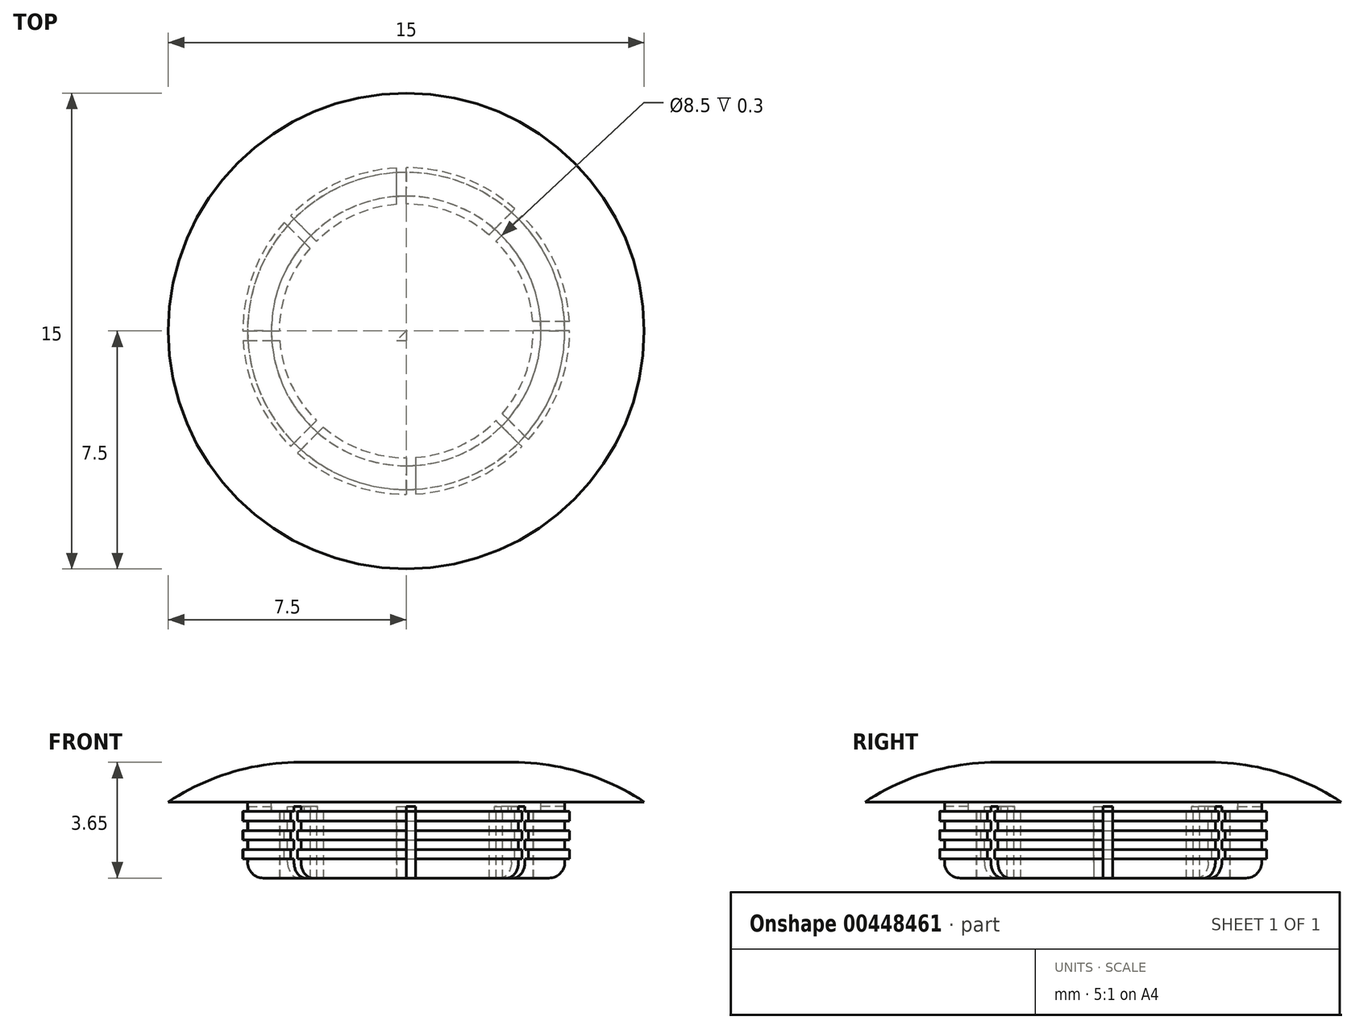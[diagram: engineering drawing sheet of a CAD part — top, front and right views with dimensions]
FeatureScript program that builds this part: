
annotation { "Feature Type Name" : "Feature", "Feature Type Description" : "" }
export const myFeature = defineFeature(function(context is Context, id is Id, definition is map)
    precondition{}
    {
        {
            var Q0;
            Q0=qCreatedBy(makeId("Top.planeOp"),FACE);
            var sketch = newSketch(context, id + "F0", { "sketchPlane" : qUnion([Q0])});
            skCircle(sketch, "E0", {"center": v(0, 0) * mm, "radius": 7.5 * mm});
            skCircle(sketch, "E1", {"center": v(0, 0) * mm, "radius": 5 * mm});
            skCircle(sketch, "E2", {"center": v(0, 0) * mm, "radius": 4.25 * mm});
            skSolve(sketch);
        }
        {
            var Q0;
            Q0=makeQuery(id+"F0.imprint","IMPRINT",FACE,{"disambiguationData":[TD([[makeQuery(id+"F0.imprint","IMPRINT",EDGE,{"derivedFrom":sQuery(id+"F0.wireOp",EDGE,"E0")}),1.0]])]});
            var Q1;
            Q1=makeQuery(id+"F0.imprint","IMPRINT",FACE,{"disambiguationData":[TD([[makeQuery(id+"F0.imprint","IMPRINT",EDGE,{"derivedFrom":sQuery(id+"F0.wireOp",EDGE,"E1")}),1.0]])]});
            var Q2;
            Q2=makeQuery(id+"F0.imprint","IMPRINT",FACE,{"disambiguationData":[TD([[makeQuery(id+"F0.imprint","IMPRINT",EDGE,{"derivedFrom":sQuery(id+"F0.wireOp",EDGE,"E2")}),1.0]])]});
            extrude(context, id + "F1", {"entities" : qUnion([Q0, Q1, Q2]), "depth" : 1.25 * mm});
        }
        {
            var Q0;
            Q0=makeQuery(id+"F1.opExtrude","CAP_EDGE",EDGE,{"disambiguationData":[OSD([sQuery(id+"F0.wireOp",EDGE,"E0")])],"isStart":false});
            fillet(context, id + "F2", {"entities" : qUnion([Q0]), "radius" : 7.5 * mm, "tangentPropagation" : true, "allowEdgeOverflow" : false});
        }
        {
            var Q0;
            Q0=makeQuery(id+"F0.imprint","IMPRINT",FACE,{"disambiguationData":[TD([[makeQuery(id+"F0.imprint","IMPRINT",EDGE,{"derivedFrom":sQuery(id+"F0.wireOp",EDGE,"E1")}),1.0]])]});
            extrude(context, id + "F3", {"entities" : qUnion([Q0]), "operationType" : NewBodyOperationType.ADD, "oppositeDirection" : true, "depth" : .3 * mm});
        }
        {
            var Q0;
            Q0=makeQuery(id+"F3.opExtrude","CAP_FACE",FACE,{"disambiguationData":[OSD([sQuery(id+"F0.wireOp",EDGE,"E1"),sQuery(id+"F0.wireOp",EDGE,"E2")])],"isStart":false});
            var sketch = newSketch(context, id + "F4", { "sketchPlane" : qUnion([Q0])});
            skCircle(sketch, "E3", {"center": v(0, 0) * mm, "radius": 5.15 * mm});
            skSolve(sketch);
        }
        {
            var Q0;
            Q0 = qSketchRegion(id + "F4", true);
            extrude(context, id + "F5", {"entities" : qUnion([Q0]), "operationType" : NewBodyOperationType.ADD, "depth" : .3 * mm});
        }
        {
            var Q0;
            Q0=makeQuery(id+"F5.opExtrude","CAP_FACE",FACE,{"disambiguationData":[OSD([sQuery(id+"F4.wireOp",EDGE,"E3")])],"isStart":false});
            var sketch = newSketch(context, id + "F6", { "sketchPlane" : qUnion([Q0])});
            skCircle(sketch, "E4", {"center": v(0, 0) * mm, "radius": 5 * mm});
            skSolve(sketch);
        }
        {
            var Q0;
            Q0 = qSketchRegion(id + "F6", true);
            extrude(context, id + "F7", {"entities" : qUnion([Q0]), "operationType" : NewBodyOperationType.ADD, "depth" : .3 * mm});
        }
        {
            var Q0;
            Q0=makeQuery(id+"F7.opExtrude","CAP_FACE",FACE,{"disambiguationData":[OSD([sQuery(id+"F6.wireOp",EDGE,"E4")])],"isStart":false});
            var sketch = newSketch(context, id + "F8", { "sketchPlane" : qUnion([Q0])});
            skCircle(sketch, "E5", {"center": v(0, 0) * mm, "radius": 5.15 * mm});
            skSolve(sketch);
        }
        {
            var Q0;
            Q0 = qSketchRegion(id + "F8", true);
            extrude(context, id + "F9", {"entities" : qUnion([Q0]), "operationType" : NewBodyOperationType.ADD, "depth" : .3 * mm});
        }
        {
            var Q0;
            Q0=makeQuery(id+"F9.opExtrude","CAP_FACE",FACE,{"disambiguationData":[OSD([sQuery(id+"F8.wireOp",EDGE,"E5")])],"isStart":false});
            var sketch = newSketch(context, id + "F10", { "sketchPlane" : qUnion([Q0])});
            skCircle(sketch, "E6", {"center": v(0, 0) * mm, "radius": 5 * mm});
            skSolve(sketch);
        }
        {
            var Q0;
            Q0 = qSketchRegion(id + "F10", true);
            extrude(context, id + "F11", {"entities" : qUnion([Q0]), "operationType" : NewBodyOperationType.ADD, "depth" : .3 * mm});
        }
        {
            var Q0;
            Q0=makeQuery(id+"F11.opExtrude","CAP_FACE",FACE,{"disambiguationData":[OSD([sQuery(id+"F10.wireOp",EDGE,"E6")])],"isStart":false});
            var sketch = newSketch(context, id + "F12", { "sketchPlane" : qUnion([Q0])});
            skCircle(sketch, "E7", {"center": v(0, 0) * mm, "radius": 5.15 * mm});
            skSolve(sketch);
        }
        {
            var Q0;
            Q0 = qSketchRegion(id + "F12", true);
            extrude(context, id + "F13", {"entities" : qUnion([Q0]), "operationType" : NewBodyOperationType.ADD, "depth" : .3 * mm});
        }
        {
            var Q0;
            Q0=makeQuery(id+"F13.opExtrude","CAP_FACE",FACE,{"disambiguationData":[OSD([sQuery(id+"F12.wireOp",EDGE,"E7")])],"isStart":false});
            var sketch = newSketch(context, id + "F14", { "sketchPlane" : qUnion([Q0])});
            skCircle(sketch, "E8", {"center": v(0, 0) * mm, "radius": 5 * mm});
            skSolve(sketch);
        }
        {
            var Q0;
            Q0 = qSketchRegion(id + "F14", true);
            extrude(context, id + "F15", {"entities" : qUnion([Q0]), "operationType" : NewBodyOperationType.ADD, "depth" : .6 * mm});
        }
        {
            var Q0;
            Q0=makeQuery(id+"F15.opExtrude","CAP_FACE",FACE,{"disambiguationData":[OSD([sQuery(id+"F14.wireOp",EDGE,"E8")])],"isStart":false});
            fillet(context, id + "F16", {"entities" : qUnion([Q0]), "radius" : .5 * mm, "tangentPropagation" : true, "allowEdgeOverflow" : false});
        }
        {
            var Q0;
            Q0=makeQuery(id+"F15.opExtrude","CAP_FACE",FACE,{"disambiguationData":[OSD([sQuery(id+"F14.wireOp",EDGE,"E8")])],"isStart":false});
            var sketch = newSketch(context, id + "F17", { "sketchPlane" : qUnion([Q0])});
            skCircle(sketch, "E9", {"center": v(0, 0) * mm, "radius": 4 * mm});
            skLineSegment(sketch, "E10", {"start": v(0, 0) * mm, "end": v(0, 6) * mm});
            skLineSegment(sketch, "E11", {"start": v(0, 0) * mm, "end": v(-4.24, 4.24) * mm});
            skLineSegment(sketch, "E12", {"start": v(-4.24, 4.24) * mm, "end": v(0, 0) * mm});
            skLineSegment(sketch, "E13", {"start": v(-6, 0) * mm, "end": v(0, 0) * mm});
            skLineSegment(sketch, "E14.MirrorCS", {"start": v(0, 0) * mm, "end": v(0, -6) * mm});
            skLineSegment(sketch, "E15.MirrorCS", {"start": v(-4.24, -4.24) * mm, "end": v(0, 0) * mm});
            skLineSegment(sketch, "E16.MirrorCS", {"start": v(4.24, 4.24) * mm, "end": v(0, 0) * mm});
            skLineSegment(sketch, "E17.MirrorCS", {"start": v(6, 0) * mm, "end": v(0, 0) * mm});
            skLineSegment(sketch, "E18.MirrorCS", {"start": v(4.24, -4.24) * mm, "end": v(0, 0) * mm});
            skLineSegment(sketch, "E19.0", {"start": v(0.3, 0) * mm, "end": v(0.3, 6) * mm});
            skLineSegment(sketch, "E20.0", {"start": v(6, -0.3) * mm, "end": v(0, -0.3) * mm});
            skLineSegment(sketch, "E21.0", {"start": v(4.03, -4.45) * mm, "end": v(-0.21, -0.21) * mm});
            skLineSegment(sketch, "E22.0", {"start": v(-0.3, 0) * mm, "end": v(-0.3, -6) * mm});
            skLineSegment(sketch, "E23.0", {"start": v(-4.45, -4.03) * mm, "end": v(-0.21, 0.21) * mm});
            skLineSegment(sketch, "E24.0", {"start": v(-6, 0.3) * mm, "end": v(0, 0.3) * mm});
            skLineSegment(sketch, "E25.0", {"start": v(-4.03, 4.45) * mm, "end": v(0.21, 0.21) * mm});
            skLineSegment(sketch, "E26.0", {"start": v(4.45, 4.03) * mm, "end": v(0.21, -0.21) * mm});
            skLineSegment(sketch, "E27", {"start": v(-4.24, 4.24) * mm, "end": v(-4.03, 4.45) * mm});
            skLineSegment(sketch, "E28", {"start": v(0, 6) * mm, "end": v(0.3, 6) * mm});
            skLineSegment(sketch, "E29", {"start": v(4.24, 4.24) * mm, "end": v(4.45, 4.03) * mm});
            skLineSegment(sketch, "E30", {"start": v(6, 0) * mm, "end": v(6, -0.3) * mm});
            skLineSegment(sketch, "E31", {"start": v(4.24, -4.24) * mm, "end": v(4.03, -4.45) * mm});
            skLineSegment(sketch, "E32", {"start": v(0, -6) * mm, "end": v(-0.3, -6) * mm});
            skLineSegment(sketch, "E33", {"start": v(-4.24, -4.24) * mm, "end": v(-4.45, -4.03) * mm});
            skLineSegment(sketch, "E34", {"start": v(-6, 0) * mm, "end": v(-6, 0.3) * mm});
            skSolve(sketch);
        }
        {
            var Q0;
            Q0=makeQuery(id+"F17.imprint","IMPRINT",FACE,{"disambiguationData":[TD([[makeQuery(id+"F17.imprint","IMPRINT",EDGE,{"derivedFrom":sQuery(id+"F17.wireOp",EDGE,"E9")}),1.0]])]});
            var Q1;
            {var subQ1=sQuery(id+"F17.wireOp",EDGE,"E9");var subQ7=sQuery(id+"F17.wireOp",EDGE,"E25.0");var subQ9=makeQuery(id+"F17.imprint","INTERSECT",VERTEX,{"derivedFrom":[subQ1,subQ7]});Q1=makeQuery(id+"F17.imprint","IMPRINT",FACE,{"disambiguationData":[TD([[makeQuery(id+"F17.imprint","IMPRINT",EDGE,{"disambiguationData":[TD([[subQ9,-1.0]])],"derivedFrom":subQ1}),1.0]])]});}
            var Q2;
            {var subQ0=sQuery(id+"F17.wireOp",EDGE,"E19.0");var subQ1=sQuery(id+"F17.wireOp",EDGE,"E9");var subQ2=makeQuery(id+"F17.imprint","INTERSECT",VERTEX,{"derivedFrom":[subQ1,subQ0]});Q2=makeQuery(id+"F17.imprint","IMPRINT",FACE,{"disambiguationData":[TD([[makeQuery(id+"F17.imprint","IMPRINT",EDGE,{"disambiguationData":[TD([[subQ2,-1.0]])],"derivedFrom":subQ1}),1.0]])]});}
            var Q3;
            {var subQ5=sQuery(id+"F17.wireOp",EDGE,"E9");var subQ7=sQuery(id+"F17.wireOp",EDGE,"E26.0");var subQ8=makeQuery(id+"F17.imprint","INTERSECT",VERTEX,{"derivedFrom":[subQ5,subQ7]});Q3=makeQuery(id+"F17.imprint","IMPRINT",FACE,{"disambiguationData":[TD([[makeQuery(id+"F17.imprint","IMPRINT",EDGE,{"disambiguationData":[TD([[subQ8,-1.0]])],"derivedFrom":subQ5}),1.0]])]});}
            var Q4;
            {var subQ1=sQuery(id+"F17.wireOp",EDGE,"E9");var subQ5=sQuery(id+"F17.wireOp",EDGE,"E17.MirrorCS");var subQ6=makeQuery(id+"F17.imprint","INTERSECT",VERTEX,{"derivedFrom":[subQ1,subQ5]});Q4=makeQuery(id+"F17.imprint","IMPRINT",FACE,{"disambiguationData":[TD([[makeQuery(id+"F17.imprint","IMPRINT",EDGE,{"disambiguationData":[TD([[subQ6,1.0]])],"derivedFrom":subQ1}),1.0]])]});}
            var Q5;
            {var subQ1=sQuery(id+"F17.wireOp",EDGE,"E9");var subQ7=sQuery(id+"F17.wireOp",EDGE,"E21.0");var subQ9=makeQuery(id+"F17.imprint","INTERSECT",VERTEX,{"derivedFrom":[subQ1,subQ7]});Q5=makeQuery(id+"F17.imprint","IMPRINT",FACE,{"disambiguationData":[TD([[makeQuery(id+"F17.imprint","IMPRINT",EDGE,{"disambiguationData":[TD([[subQ9,-1.0]])],"derivedFrom":subQ1}),1.0]])]});}
            var Q6;
            {var subQ3=sQuery(id+"F17.wireOp",EDGE,"E22.0");var subQ7=sQuery(id+"F17.wireOp",EDGE,"E9");var subQ9=makeQuery(id+"F17.imprint","INTERSECT",VERTEX,{"derivedFrom":[subQ7,subQ3]});Q6=makeQuery(id+"F17.imprint","IMPRINT",FACE,{"disambiguationData":[TD([[makeQuery(id+"F17.imprint","IMPRINT",EDGE,{"disambiguationData":[TD([[subQ9,-1.0]])],"derivedFrom":subQ7}),1.0]])]});}
            var Q7;
            {var subQ5=sQuery(id+"F17.wireOp",EDGE,"E9");var subQ7=sQuery(id+"F17.wireOp",EDGE,"E23.0");var subQ9=makeQuery(id+"F17.imprint","INTERSECT",VERTEX,{"derivedFrom":[subQ5,subQ7]});Q7=makeQuery(id+"F17.imprint","IMPRINT",FACE,{"disambiguationData":[TD([[makeQuery(id+"F17.imprint","IMPRINT",EDGE,{"disambiguationData":[TD([[subQ9,-1.0]])],"derivedFrom":subQ5}),1.0]])]});}
            var Q8;
            {var subQ1=sQuery(id+"F17.wireOp",EDGE,"E9");var subQ7=sQuery(id+"F17.wireOp",EDGE,"E24.0");var subQ8=makeQuery(id+"F17.imprint","INTERSECT",VERTEX,{"derivedFrom":[subQ1,subQ7]});Q8=makeQuery(id+"F17.imprint","IMPRINT",FACE,{"disambiguationData":[TD([[makeQuery(id+"F17.imprint","IMPRINT",EDGE,{"disambiguationData":[TD([[subQ8,-1.0]])],"derivedFrom":subQ1}),1.0]])]});}
            var Q9;
            {var subQ0=sQuery(id+"F17.wireOp",EDGE,"E17.MirrorCS");var subQ1=makeQuery(id+"F17.imprint","INTERSECT",VERTEX,{"derivedFrom":[subQ0,sQuery(id+"F17.wireOp",EDGE,"E19.0")]});Q9=makeQuery(id+"F17.imprint","IMPRINT",FACE,{"disambiguationData":[TD([[makeQuery(id+"F17.imprint","IMPRINT",EDGE,{"disambiguationData":[TD([[subQ1,1.0]])],"derivedFrom":subQ0}),1.0]])]});}
            var Q10;
            {var subQ0=sQuery(id+"F17.wireOp",EDGE,"E16.MirrorCS");var subQ1=makeQuery(id+"F17.imprint","INTERSECT",VERTEX,{"derivedFrom":[subQ0,sQuery(id+"F17.wireOp",EDGE,"E25.0")]});Q10=makeQuery(id+"F17.imprint","IMPRINT",FACE,{"disambiguationData":[TD([[makeQuery(id+"F17.imprint","IMPRINT",EDGE,{"disambiguationData":[TD([[subQ1,1.0]])],"derivedFrom":subQ0}),1.0]])]});}
            var Q11;
            {var subQ1=sQuery(id+"F17.wireOp",EDGE,"E10");var subQ3=makeQuery(id+"F17.imprint","INTERSECT",VERTEX,{"derivedFrom":[subQ1,sQuery(id+"F17.wireOp",EDGE,"E24.0")]});Q11=makeQuery(id+"F17.imprint","IMPRINT",FACE,{"disambiguationData":[TD([[makeQuery(id+"F17.imprint","IMPRINT",EDGE,{"disambiguationData":[TD([[subQ3,-1.0]])],"derivedFrom":subQ1}),-1.0]])]});}
            var Q12;
            {var subQ0=sQuery(id+"F17.wireOp",EDGE,"E12");var subQ5=makeQuery(id+"F17.imprint","INTERSECT",VERTEX,{"derivedFrom":[subQ0,sQuery(id+"F17.wireOp",EDGE,"E23.0")]});Q12=makeQuery(id+"F17.imprint","IMPRINT",FACE,{"disambiguationData":[TD([[makeQuery(id+"F17.imprint","IMPRINT",EDGE,{"disambiguationData":[TD([[subQ5,1.0]])],"derivedFrom":subQ0}),1.0]])]});}
            var Q13;
            {var subQ0=sQuery(id+"F17.wireOp",EDGE,"E13");var subQ5=makeQuery(id+"F17.imprint","INTERSECT",VERTEX,{"derivedFrom":[subQ0,sQuery(id+"F17.wireOp",EDGE,"E22.0")]});Q13=makeQuery(id+"F17.imprint","IMPRINT",FACE,{"disambiguationData":[TD([[makeQuery(id+"F17.imprint","IMPRINT",EDGE,{"disambiguationData":[TD([[subQ5,1.0]])],"derivedFrom":subQ0}),1.0]])]});}
            var Q14;
            {var subQ0=sQuery(id+"F17.wireOp",EDGE,"E15.MirrorCS");var subQ6=makeQuery(id+"F17.imprint","INTERSECT",VERTEX,{"derivedFrom":[subQ0,sQuery(id+"F17.wireOp",EDGE,"E21.0")]});Q14=makeQuery(id+"F17.imprint","IMPRINT",FACE,{"disambiguationData":[TD([[makeQuery(id+"F17.imprint","IMPRINT",EDGE,{"disambiguationData":[TD([[subQ6,1.0]])],"derivedFrom":subQ0}),1.0]])]});}
            var Q15;
            {var subQ1=sQuery(id+"F17.wireOp",EDGE,"E14.MirrorCS");var subQ3=makeQuery(id+"F17.imprint","INTERSECT",VERTEX,{"derivedFrom":[subQ1,sQuery(id+"F17.wireOp",EDGE,"E20.0")]});Q15=makeQuery(id+"F17.imprint","IMPRINT",FACE,{"disambiguationData":[TD([[makeQuery(id+"F17.imprint","IMPRINT",EDGE,{"disambiguationData":[TD([[subQ3,-1.0]])],"derivedFrom":subQ1}),-1.0]])]});}
            var Q16;
            {var subQ0=sQuery(id+"F17.wireOp",EDGE,"E18.MirrorCS");var subQ6=makeQuery(id+"F17.imprint","INTERSECT",VERTEX,{"derivedFrom":[subQ0,sQuery(id+"F17.wireOp",EDGE,"E26.0")]});Q16=makeQuery(id+"F17.imprint","IMPRINT",FACE,{"disambiguationData":[TD([[makeQuery(id+"F17.imprint","IMPRINT",EDGE,{"disambiguationData":[TD([[subQ6,1.0]])],"derivedFrom":subQ0}),1.0]])]});}
            var Q17;
            {var subQ0=sQuery(id+"F17.wireOp",EDGE,"E27");Q17=makeQuery(id+"F17.imprint","IMPRINT",FACE,{"disambiguationData":[TD([[makeQuery(id+"F17.imprint","IMPRINT",EDGE,{"derivedFrom":subQ0}),-1.0]])]});}
            var Q18;
            {var subQ0=sQuery(id+"F17.wireOp",EDGE,"E25.0");var subQ1=sQuery(id+"F17.wireOp",EDGE,"E9");var subQ2=makeQuery(id+"F17.imprint","INTERSECT",VERTEX,{"derivedFrom":[subQ1,subQ0]});Q18=makeQuery(id+"F17.imprint","IMPRINT",FACE,{"disambiguationData":[TD([[makeQuery(id+"F17.imprint","IMPRINT",EDGE,{"disambiguationData":[TD([[subQ2,-1.0]])],"derivedFrom":subQ1}),-1.0]])]});}
            var Q19;
            {var subQ0=sQuery(id+"F17.wireOp",EDGE,"E34");Q19=makeQuery(id+"F17.imprint","IMPRINT",FACE,{"disambiguationData":[TD([[makeQuery(id+"F17.imprint","IMPRINT",EDGE,{"derivedFrom":subQ0}),-1.0]])]});}
            var Q20;
            {var subQ0=sQuery(id+"F17.wireOp",EDGE,"E24.0");var subQ1=sQuery(id+"F17.wireOp",EDGE,"E9");var subQ2=makeQuery(id+"F17.imprint","INTERSECT",VERTEX,{"derivedFrom":[subQ1,subQ0]});Q20=makeQuery(id+"F17.imprint","IMPRINT",FACE,{"disambiguationData":[TD([[makeQuery(id+"F17.imprint","IMPRINT",EDGE,{"disambiguationData":[TD([[subQ2,-1.0]])],"derivedFrom":subQ1}),-1.0]])]});}
            var Q21;
            {var subQ0=sQuery(id+"F17.wireOp",EDGE,"E33");Q21=makeQuery(id+"F17.imprint","IMPRINT",FACE,{"disambiguationData":[TD([[makeQuery(id+"F17.imprint","IMPRINT",EDGE,{"derivedFrom":subQ0}),-1.0]])]});}
            var Q22;
            {var subQ0=sQuery(id+"F17.wireOp",EDGE,"E23.0");var subQ1=sQuery(id+"F17.wireOp",EDGE,"E9");var subQ2=makeQuery(id+"F17.imprint","INTERSECT",VERTEX,{"derivedFrom":[subQ1,subQ0]});Q22=makeQuery(id+"F17.imprint","IMPRINT",FACE,{"disambiguationData":[TD([[makeQuery(id+"F17.imprint","IMPRINT",EDGE,{"disambiguationData":[TD([[subQ2,-1.0]])],"derivedFrom":subQ1}),-1.0]])]});}
            var Q23;
            {var subQ0=sQuery(id+"F17.wireOp",EDGE,"E32");Q23=makeQuery(id+"F17.imprint","IMPRINT",FACE,{"disambiguationData":[TD([[makeQuery(id+"F17.imprint","IMPRINT",EDGE,{"derivedFrom":subQ0}),-1.0]])]});}
            var Q24;
            {var subQ0=sQuery(id+"F17.wireOp",EDGE,"E22.0");var subQ1=sQuery(id+"F17.wireOp",EDGE,"E9");var subQ2=makeQuery(id+"F17.imprint","INTERSECT",VERTEX,{"derivedFrom":[subQ1,subQ0]});Q24=makeQuery(id+"F17.imprint","IMPRINT",FACE,{"disambiguationData":[TD([[makeQuery(id+"F17.imprint","IMPRINT",EDGE,{"disambiguationData":[TD([[subQ2,-1.0]])],"derivedFrom":subQ1}),-1.0]])]});}
            var Q25;
            {var subQ0=sQuery(id+"F17.wireOp",EDGE,"E31");Q25=makeQuery(id+"F17.imprint","IMPRINT",FACE,{"disambiguationData":[TD([[makeQuery(id+"F17.imprint","IMPRINT",EDGE,{"derivedFrom":subQ0}),-1.0]])]});}
            var Q26;
            {var subQ0=sQuery(id+"F17.wireOp",EDGE,"E21.0");var subQ1=sQuery(id+"F17.wireOp",EDGE,"E9");var subQ2=makeQuery(id+"F17.imprint","INTERSECT",VERTEX,{"derivedFrom":[subQ1,subQ0]});Q26=makeQuery(id+"F17.imprint","IMPRINT",FACE,{"disambiguationData":[TD([[makeQuery(id+"F17.imprint","IMPRINT",EDGE,{"disambiguationData":[TD([[subQ2,-1.0]])],"derivedFrom":subQ1}),-1.0]])]});}
            var Q27;
            {var subQ0=sQuery(id+"F17.wireOp",EDGE,"E30");Q27=makeQuery(id+"F17.imprint","IMPRINT",FACE,{"disambiguationData":[TD([[makeQuery(id+"F17.imprint","IMPRINT",EDGE,{"derivedFrom":subQ0}),-1.0]])]});}
            var Q28;
            {var subQ0=sQuery(id+"F17.wireOp",EDGE,"E17.MirrorCS");var subQ1=sQuery(id+"F17.wireOp",EDGE,"E9");var subQ2=makeQuery(id+"F17.imprint","INTERSECT",VERTEX,{"derivedFrom":[subQ1,subQ0]});Q28=makeQuery(id+"F17.imprint","IMPRINT",FACE,{"disambiguationData":[TD([[makeQuery(id+"F17.imprint","IMPRINT",EDGE,{"disambiguationData":[TD([[subQ2,1.0]])],"derivedFrom":subQ1}),-1.0]])]});}
            var Q29;
            {var subQ0=sQuery(id+"F17.wireOp",EDGE,"E29");Q29=makeQuery(id+"F17.imprint","IMPRINT",FACE,{"disambiguationData":[TD([[makeQuery(id+"F17.imprint","IMPRINT",EDGE,{"derivedFrom":subQ0}),-1.0]])]});}
            var Q30;
            {var subQ0=sQuery(id+"F17.wireOp",EDGE,"E26.0");var subQ1=sQuery(id+"F17.wireOp",EDGE,"E9");var subQ2=makeQuery(id+"F17.imprint","INTERSECT",VERTEX,{"derivedFrom":[subQ1,subQ0]});Q30=makeQuery(id+"F17.imprint","IMPRINT",FACE,{"disambiguationData":[TD([[makeQuery(id+"F17.imprint","IMPRINT",EDGE,{"disambiguationData":[TD([[subQ2,-1.0]])],"derivedFrom":subQ1}),-1.0]])]});}
            var Q31;
            {var subQ0=sQuery(id+"F17.wireOp",EDGE,"E28");Q31=makeQuery(id+"F17.imprint","IMPRINT",FACE,{"disambiguationData":[TD([[makeQuery(id+"F17.imprint","IMPRINT",EDGE,{"derivedFrom":subQ0}),-1.0]])]});}
            var Q32;
            {var subQ0=sQuery(id+"F17.wireOp",EDGE,"E19.0");var subQ1=sQuery(id+"F17.wireOp",EDGE,"E9");var subQ2=makeQuery(id+"F17.imprint","INTERSECT",VERTEX,{"derivedFrom":[subQ1,subQ0]});Q32=makeQuery(id+"F17.imprint","IMPRINT",FACE,{"disambiguationData":[TD([[makeQuery(id+"F17.imprint","IMPRINT",EDGE,{"disambiguationData":[TD([[subQ2,-1.0]])],"derivedFrom":subQ1}),-1.0]])]});}
            extrude(context, id + "F18", {"entities" : qUnion([Q0, Q1, Q2, Q3, Q4, Q5, Q6, Q7, Q8, Q9, Q10, Q11, Q12, Q13, Q14, Q15, Q16, Q17, Q18, Q19, Q20, Q21, Q22, Q23, Q24, Q25, Q26, Q27, Q28, Q29, Q30, Q31, Q32]), "operationType" : NewBodyOperationType.REMOVE, "oppositeDirection" : true, "depth" : 2.25 * mm});
        }
    });
